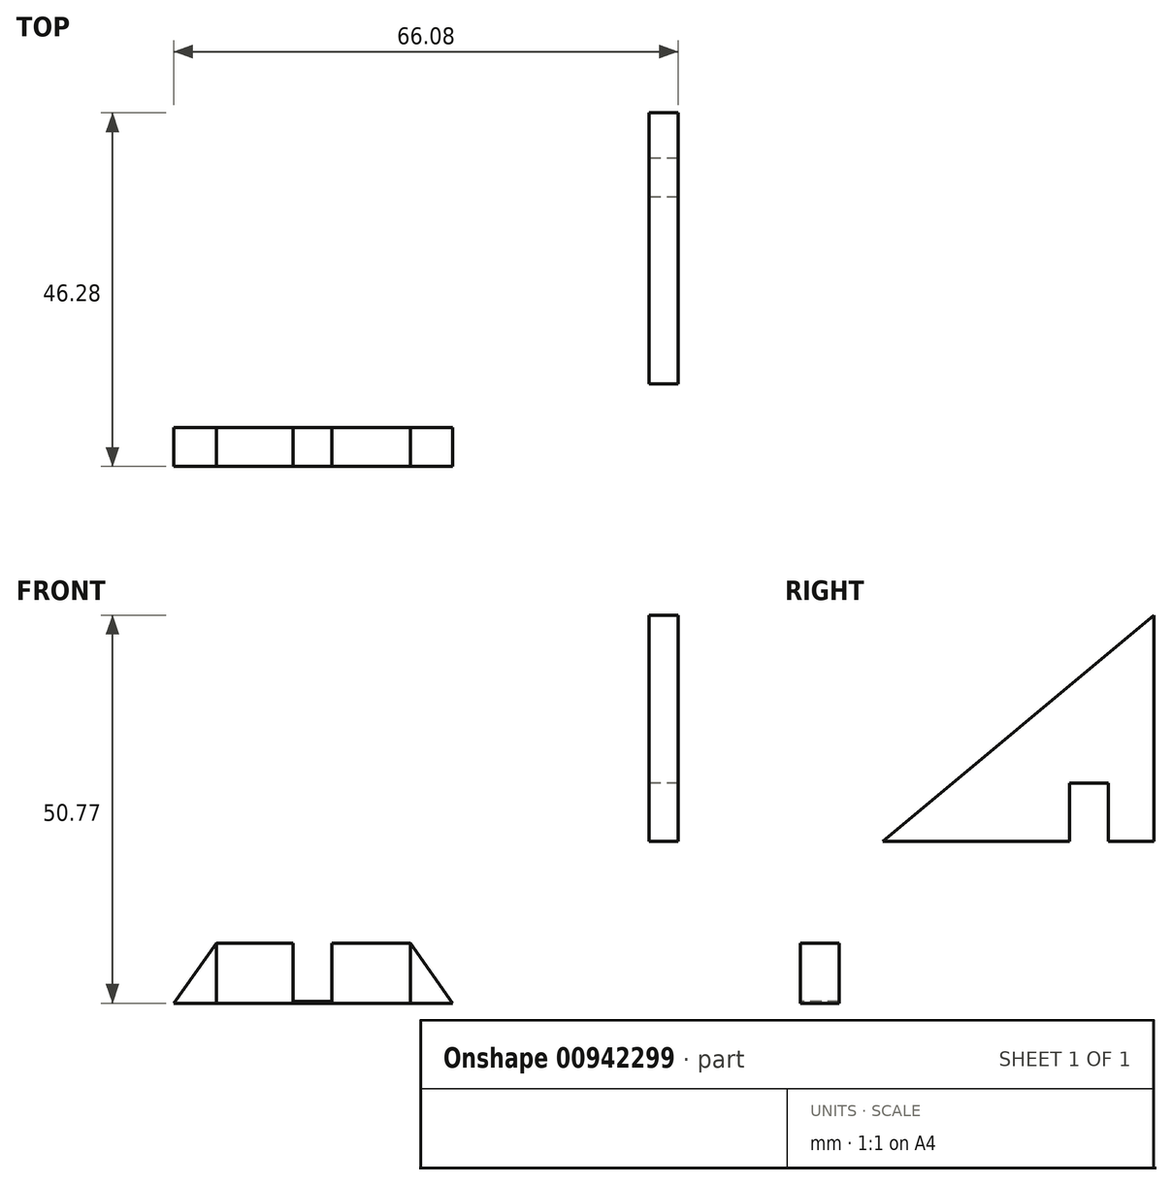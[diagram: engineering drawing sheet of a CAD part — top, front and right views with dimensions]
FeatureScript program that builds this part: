
annotation { "Feature Type Name" : "Feature", "Feature Type Description" : "" }
export const myFeature = defineFeature(function(context is Context, id is Id, definition is map)
    precondition{}
    {
        {
            var Q0;
            Q0=qCreatedBy(makeId("Right.planeOp"),FACE);
            var sketch = newSketch(context, id + "F0", { "sketchPlane" : qUnion([Q0])});
            skLineSegment(sketch, "E0", {"start": v(41.2, 29.57) * mm, "end": v(41.2, 0) * mm});
            skLineSegment(sketch, "E1", {"start": v(41.2, 0) * mm, "end": v(5.71, 0) * mm});
            skLineSegment(sketch, "E2", {"start": v(5.71, 0) * mm, "end": v(41.2, 29.57) * mm});
            skSolve(sketch);
        }
        {
            var Q0;
            Q0 = qSketchRegion(id + "F0", true);
            extrude(context, id + "F1", {"entities" : qUnion([Q0]), "depth" : 3.8 * mm, "offsetDistance" : 25.4 * mm});
        }
        {
            var Q0;
            Q0=makeQuery(id+"F1.opExtrude","CAP_FACE",FACE,{"disambiguationData":[OSD([sQuery(id+"F0.wireOp",EDGE,"E0"),sQuery(id+"F0.wireOp",EDGE,"E1"),sQuery(id+"F0.wireOp",EDGE,"E2")])],"isStart":true});
            var sketch = newSketch(context, id + "F2", { "sketchPlane" : qUnion([Q0])});
            skLineSegment(sketch, "E3.bottom", {"start": v(-35.24, 7.62) * mm, "end": v(-30.16, 7.62) * mm});
            skLineSegment(sketch, "E3.top", {"start": v(-35.24, 0) * mm, "end": v(-30.16, 0) * mm});
            skLineSegment(sketch, "E3.left", {"start": v(-35.24, 7.62) * mm, "end": v(-35.24, 0) * mm});
            skLineSegment(sketch, "E3.right", {"start": v(-30.16, 7.62) * mm, "end": v(-30.16, 0) * mm});
            skSolve(sketch);
        }
        {
            var Q0;
            Q0 = qSketchRegion(id + "F2", true);
            extrude(context, id + "F3", {"entities" : qUnion([Q0]), "operationType" : NewBodyOperationType.REMOVE, "oppositeDirection" : true, "depth" : 25.4 * mm, "offsetDistance" : 25.4 * mm});
        }
        {
            var Q0;
            Q0=qCreatedBy(makeId("Front.planeOp"),FACE);
            var sketch = newSketch(context, id + "F4", { "sketchPlane" : qUnion([Q0])});
            skLineSegment(sketch, "E4.bottom", {"start": v(-56.68, -13.32) * mm, "end": v(-31.28, -13.32) * mm});
            skLineSegment(sketch, "E4.top", {"start": v(-56.68, -21.2) * mm, "end": v(-31.28, -21.2) * mm});
            skLineSegment(sketch, "E4.left", {"start": v(-56.68, -13.32) * mm, "end": v(-56.68, -21.2) * mm});
            skLineSegment(sketch, "E4.right", {"start": v(-31.28, -13.32) * mm, "end": v(-31.28, -21.2) * mm});
            skLineSegment(sketch, "E5", {"start": v(-56.68, -13.32) * mm, "end": v(-62.27, -21.2) * mm});
            skLineSegment(sketch, "E6", {"start": v(-62.27, -21.2) * mm, "end": v(-56.68, -21.2) * mm});
            skLineSegment(sketch, "E7", {"start": v(-31.28, -13.32) * mm, "end": v(-25.7, -21.2) * mm});
            skLineSegment(sketch, "E8", {"start": v(-31.28, -21.2) * mm, "end": v(-25.7, -21.2) * mm});
            skSolve(sketch);
        }
        {
            var Q0;
            Q0=makeQuery(id+"F4.imprint","IMPRINT",FACE,{"disambiguationData":[TD([[makeQuery(id+"F4.imprint","IMPRINT",EDGE,{"derivedFrom":sQuery(id+"F4.wireOp",EDGE,"E4.bottom")}),-1.0]])]});
            var sketch = newSketch(context, id + "F5", { "sketchPlane" : qUnion([Q0])});
            skSolve(sketch);
        }
        {
            var Q0;
            Q0=makeQuery(id+"F4.imprint","IMPRINT",FACE,{"disambiguationData":[TD([[makeQuery(id+"F4.imprint","IMPRINT",EDGE,{"derivedFrom":sQuery(id+"F4.wireOp",EDGE,"E4.left")}),-1.0]])]});
            var Q1;
            Q1=makeQuery(id+"F5.imprint","IMPRINT",FACE,{"disambiguationData":[TD([[makeQuery(id+"F5.imprint","IMPRINT",EDGE,{"derivedFrom":makeQuery(id+"F4.imprint","IMPRINT",EDGE,{"derivedFrom":sQuery(id+"F4.wireOp",EDGE,"E4.bottom")})}),-1.0]])]});
            var Q2;
            Q2=makeQuery(id+"F4.imprint","IMPRINT",FACE,{"disambiguationData":[TD([[makeQuery(id+"F4.imprint","IMPRINT",EDGE,{"derivedFrom":sQuery(id+"F4.wireOp",EDGE,"E4.right")}),1.0]])]});
            extrude(context, id + "F6", {"entities" : qUnion([Q0, Q1, Q2]), "depth" : 5.08 * mm, "offsetDistance" : 25.4 * mm});
        }
        {
            var Q0;
            Q0=makeQuery(id+"F6.opExtrude","CAP_FACE",FACE,{"disambiguationData":[OSD([sQuery(id+"F4.wireOp",EDGE,"E4.bottom"),sQuery(id+"F4.wireOp",EDGE,"E4.top"),sQuery(id+"F4.wireOp",EDGE,"E4.left"),sQuery(id+"F4.wireOp",EDGE,"E4.right")])],"isStart":false});
            var sketch = newSketch(context, id + "F7", { "sketchPlane" : qUnion([Q0])});
            skLineSegment(sketch, "E9.bottom", {"start": v(-46.6, -13.32) * mm, "end": v(-41.51, -13.32) * mm});
            skLineSegment(sketch, "E9.top", {"start": v(-46.6, -20.94) * mm, "end": v(-41.51, -20.94) * mm});
            skLineSegment(sketch, "E9.left", {"start": v(-46.6, -13.32) * mm, "end": v(-46.6, -20.94) * mm});
            skLineSegment(sketch, "E9.right", {"start": v(-41.51, -13.32) * mm, "end": v(-41.51, -20.94) * mm});
            skSolve(sketch);
        }
        {
            var Q0;
            Q0=makeQuery(id+"F7.imprint","IMPRINT",FACE,{"disambiguationData":[TD([[makeQuery(id+"F7.imprint","IMPRINT",EDGE,{"derivedFrom":sQuery(id+"F7.wireOp",EDGE,"E9.bottom")}),-1.0]])]});
            extrude(context, id + "F8", {"entities" : qUnion([Q0]), "operationType" : NewBodyOperationType.REMOVE, "oppositeDirection" : true, "depth" : 25.4 * mm, "offsetDistance" : 25.4 * mm});
        }
    });
